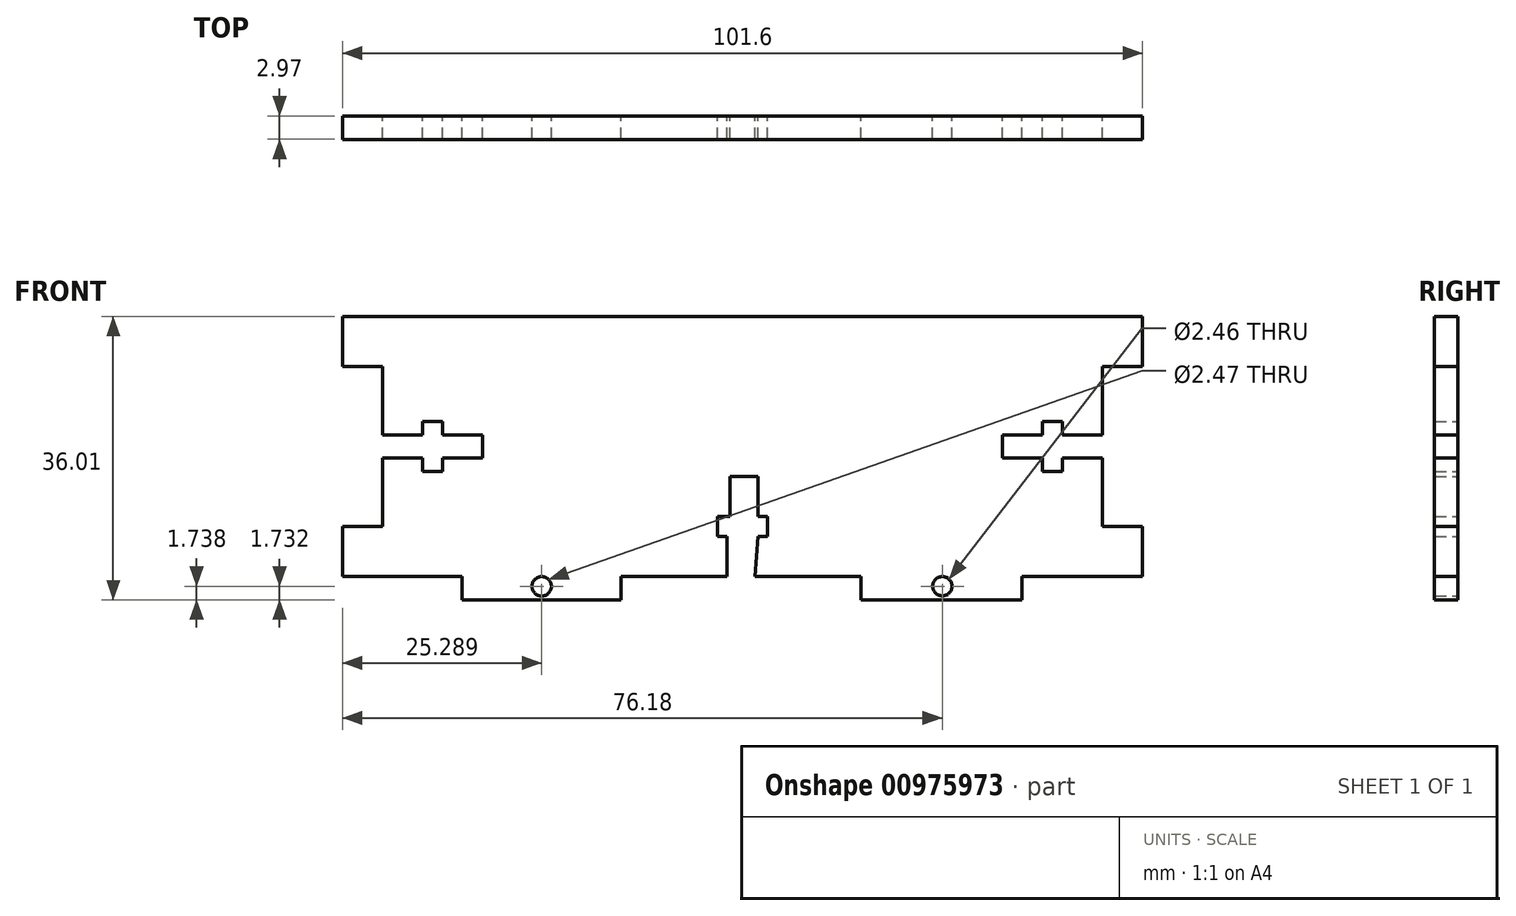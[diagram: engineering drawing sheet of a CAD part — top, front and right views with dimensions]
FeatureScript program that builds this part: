
annotation { "Feature Type Name" : "Feature", "Feature Type Description" : "" }
export const myFeature = defineFeature(function(context is Context, id is Id, definition is map)
    precondition{}
    {
        {
            var Q0;
            Q0=qCreatedBy(makeId("Front.planeOp"),FACE);
            var sketch = newSketch(context, id + "F0", { "sketchPlane" : qUnion([Q0])});
            skLineSegment(sketch, "E0.top", {"start": v(50.8, 16.52) * mm, "end": v(-50.8, 16.52) * mm});
            skPoint(sketch, "E0.middle", {"position": v(0, 0) * mm});
            skLineSegment(sketch, "E1.bottom", {"start": v(-45.73, -10.16) * mm, "end": v(-50.8, -10.16) * mm});
            skLineSegment(sketch, "E1.top", {"start": v(-45.73, 10.16) * mm, "end": v(-50.8, 10.16) * mm});
            skLineSegment(sketch, "E2.bottom", {"start": v(45.73, 10.16) * mm, "end": v(50.8, 10.16) * mm});
            skLineSegment(sketch, "E2.top", {"start": v(45.73, -10.16) * mm, "end": v(50.8, -10.16) * mm});
            skLineSegment(sketch, "E3", {"start": v(-50.8, 10.16) * mm, "end": v(-50.8, 16.52) * mm});
            skLineSegment(sketch, "E4", {"start": v(-50.8, -10.16) * mm, "end": v(-50.8, -16.52) * mm});
            skLineSegment(sketch, "E5", {"start": v(50.8, -16.52) * mm, "end": v(50.8, -10.16) * mm});
            skLineSegment(sketch, "E6", {"start": v(50.8, 10.16) * mm, "end": v(50.8, 16.52) * mm});
            skPoint(sketch, "E7", {"position": v(-39.38, 0) * mm});
            skLineSegment(sketch, "E8.right", {"start": v(-33.04, -1.46) * mm, "end": v(-33.04, 1.46) * mm});
            skLineSegment(sketch, "E9.bottom", {"start": v(-38.12, -3.17) * mm, "end": v(-40.65, -3.17) * mm});
            skLineSegment(sketch, "E9.top", {"start": v(-38.12, 3.17) * mm, "end": v(-40.65, 3.17) * mm});
            skLineSegment(sketch, "E10", {"start": v(-45.73, 1.46) * mm, "end": v(-40.65, 1.46) * mm});
            skLineSegment(sketch, "E11", {"start": v(-40.65, 1.46) * mm, "end": v(-40.65, 3.17) * mm});
            skLineSegment(sketch, "E12", {"start": v(-38.12, 3.17) * mm, "end": v(-38.12, 1.46) * mm});
            skLineSegment(sketch, "E13", {"start": v(-38.12, 1.46) * mm, "end": v(-33.04, 1.46) * mm});
            skLineSegment(sketch, "E14", {"start": v(-33.04, -1.46) * mm, "end": v(-38.12, -1.46) * mm});
            skLineSegment(sketch, "E15", {"start": v(-38.12, -1.46) * mm, "end": v(-38.12, -3.17) * mm});
            skLineSegment(sketch, "E16", {"start": v(-40.65, -3.17) * mm, "end": v(-40.65, -1.46) * mm});
            skLineSegment(sketch, "E17", {"start": v(-40.65, -1.46) * mm, "end": v(-45.73, -1.46) * mm});
            skLineSegment(sketch, "E18", {"start": v(-45.73, 10.16) * mm, "end": v(-45.73, 1.46) * mm});
            skLineSegment(sketch, "E19", {"start": v(-45.73, -1.46) * mm, "end": v(-45.73, -10.16) * mm});
            skLineSegment(sketch, "E20.MirrorCS", {"start": v(40.65, -3.17) * mm, "end": v(40.65, -1.46) * mm});
            skLineSegment(sketch, "E21.MirrorCS", {"start": v(38.12, 3.17) * mm, "end": v(38.12, 1.46) * mm});
            skLineSegment(sketch, "E22.MirrorCS", {"start": v(38.12, -1.46) * mm, "end": v(38.12, -3.17) * mm});
            skPoint(sketch, "E23.MirrorP", {"position": v(39.38, 0) * mm});
            skLineSegment(sketch, "E24.MirrorCS", {"start": v(40.65, 1.46) * mm, "end": v(40.65, 3.17) * mm});
            skLineSegment(sketch, "E25.MirrorCS", {"start": v(40.65, -1.46) * mm, "end": v(45.73, -1.46) * mm});
            skLineSegment(sketch, "E26.MirrorCS", {"start": v(33.04, -1.46) * mm, "end": v(33.04, 1.46) * mm});
            skLineSegment(sketch, "E27.MirrorCS", {"start": v(33.04, -1.46) * mm, "end": v(38.12, -1.46) * mm});
            skLineSegment(sketch, "E28.MirrorCS", {"start": v(38.12, 1.46) * mm, "end": v(33.04, 1.46) * mm});
            skLineSegment(sketch, "E29.MirrorCS", {"start": v(38.12, 3.17) * mm, "end": v(40.65, 3.17) * mm});
            skLineSegment(sketch, "E30.MirrorCS", {"start": v(45.73, 1.46) * mm, "end": v(40.65, 1.46) * mm});
            skLineSegment(sketch, "E31.MirrorCS", {"start": v(38.12, -3.17) * mm, "end": v(40.65, -3.17) * mm});
            skLineSegment(sketch, "E32", {"start": v(45.73, -10.16) * mm, "end": v(45.73, -1.46) * mm});
            skLineSegment(sketch, "E33", {"start": v(45.73, 1.46) * mm, "end": v(45.73, 10.16) * mm});
            skPoint(sketch, "E34", {"position": v(0, -10.18) * mm});
            skLineSegment(sketch, "E35.top", {"start": v(1.96, -3.83) * mm, "end": v(-1.6, -3.83) * mm});
            skLineSegment(sketch, "E36.left", {"start": v(3.17, -8.91) * mm, "end": v(3.17, -11.44) * mm});
            skLineSegment(sketch, "E36.right", {"start": v(-3.17, -8.91) * mm, "end": v(-3.17, -11.44) * mm});
            skLineSegment(sketch, "E37", {"start": v(-1.96, -16.53) * mm, "end": v(-1.96, -11.44) * mm});
            skLineSegment(sketch, "E38", {"start": v(-1.96, -11.44) * mm, "end": v(-3.17, -11.44) * mm});
            skLineSegment(sketch, "E39", {"start": v(-1.6, -3.83) * mm, "end": v(1.96, -3.83) * mm});
            skLineSegment(sketch, "E40", {"start": v(1.96, -3.83) * mm, "end": v(1.96, -8.91) * mm});
            skLineSegment(sketch, "E41", {"start": v(1.96, -8.91) * mm, "end": v(3.17, -8.91) * mm});
            skLineSegment(sketch, "E42", {"start": v(3.17, -11.44) * mm, "end": v(1.96, -11.44) * mm});
            skLineSegment(sketch, "E43", {"start": v(-3.17, -8.91) * mm, "end": v(-1.6, -8.91) * mm});
            skLineSegment(sketch, "E44", {"start": v(1.96, -11.44) * mm, "end": v(1.6, -16.53) * mm});
            skLineSegment(sketch, "E45", {"start": v(-1.6, -8.91) * mm, "end": v(-1.6, -3.83) * mm});
            skLineSegment(sketch, "E46", {"start": v(-50.8, -16.52) * mm, "end": v(-36.27, -16.52) * mm});
            skLineSegment(sketch, "E47", {"start": v(-15.42, -16.52) * mm, "end": v(-1.96, -16.53) * mm});
            skLineSegment(sketch, "E48.MirrorCS", {"start": v(15.06, -16.52) * mm, "end": v(15.06, -19.49) * mm});
            skLineSegment(sketch, "E49", {"start": v(-33.73, -19.49) * mm, "end": v(-15.99, -19.49) * mm});
            skLineSegment(sketch, "E50", {"start": v(32.8, -19.49) * mm, "end": v(15.06, -19.49) * mm});
            skLineSegment(sketch, "E51", {"start": v(-33.73, -19.49) * mm, "end": v(-35, -19.49) * mm});
            skLineSegment(sketch, "E52", {"start": v(32.8, -19.49) * mm, "end": v(34.72, -19.49) * mm});
            skLineSegment(sketch, "E53", {"start": v(-35.64, -16.52) * mm, "end": v(-36.27, -16.52) * mm});
            skLineSegment(sketch, "E54", {"start": v(36.92, -16.52) * mm, "end": v(50.8, -16.52) * mm});
            skLineSegment(sketch, "E55", {"start": v(-15.99, -19.49) * mm, "end": v(-15.42, -19.49) * mm});
            skLineSegment(sketch, "E56", {"start": v(1.6, -16.53) * mm, "end": v(15.06, -16.52) * mm});
            skLineSegment(sketch, "E57", {"start": v(-15.42, -16.52) * mm, "end": v(-15.42, -19.49) * mm});
            skLineSegment(sketch, "E58", {"start": v(-35.64, -16.52) * mm, "end": v(-35.64, -19.49) * mm});
            skLineSegment(sketch, "E59", {"start": v(-35, -19.49) * mm, "end": v(-35.64, -19.49) * mm});
            skLineSegment(sketch, "E60", {"start": v(35.51, -16.52) * mm, "end": v(35.51, -19.49) * mm});
            skLineSegment(sketch, "E61", {"start": v(35.51, -19.49) * mm, "end": v(34.72, -19.49) * mm});
            skLineSegment(sketch, "E62", {"start": v(35.51, -16.52) * mm, "end": v(36.92, -16.52) * mm});
            skPoint(sketch, "E63", {"position": v(26.83, -16.52) * mm});
            skPoint(sketch, "E64", {"position": v(23.89, -16.52) * mm});
            skLineSegment(sketch, "E65", {"start": v(26.83, -16.52) * mm, "end": v(23.89, -16.52) * mm});
            skPoint(sketch, "E66", {"position": v(25.36, -16.52) * mm});
            skLineSegment(sketch, "E67", {"start": v(25.36, -16.52) * mm, "end": v(25.36, -18.98) * mm});
            skCircle(sketch, "E68", {"center": v(25.38, -17.75) * mm, "radius": 1.23 * mm});
            skPoint(sketch, "E68.third.point", {"position": v(25.4, -18.98) * mm});
            skLineSegment(sketch, "E69", {"start": v(0.18, -3.83) * mm, "end": v(0.18, -2.3) * mm});
            skPoint(sketch, "E70", {"position": v(-25.53, -16.52) * mm});
            skLineSegment(sketch, "E71", {"start": v(-25.53, -16.52) * mm, "end": v(-25.53, -19) * mm});
            skCircle(sketch, "E72", {"center": v(-25.51, -17.76) * mm, "radius": 1.23 * mm});
            skPoint(sketch, "E72.third.point", {"position": v(-25.5, -19) * mm});
            skSolve(sketch);
        }
        {
            var Q0;
            Q0=makeQuery(id+"F0.imprint","IMPRINT",FACE,{"disambiguationData":[TD([[makeQuery(id+"F0.imprint","IMPRINT",EDGE,{"derivedFrom":sQuery(id+"F0.wireOp",EDGE,"E0.top")}),1.0]])]});
            extrude(context, id + "F1", {"entities" : qUnion([Q0]), "depth" : 2.97 * mm, "offsetDistance" : 25.4 * mm});
        }
    });
